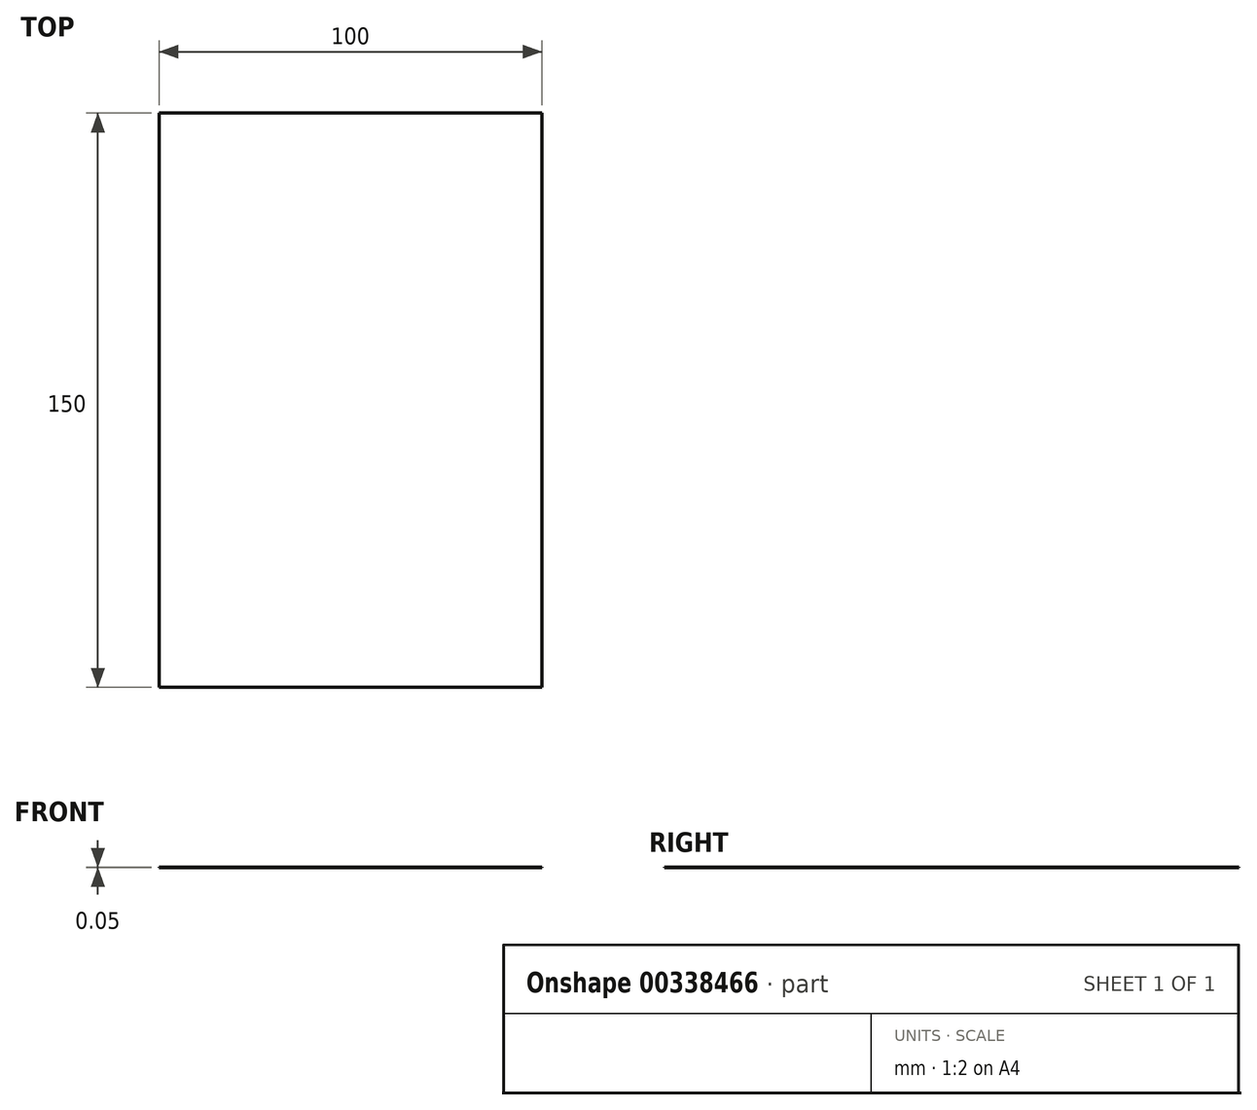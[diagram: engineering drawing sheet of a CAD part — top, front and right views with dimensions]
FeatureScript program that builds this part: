
annotation { "Feature Type Name" : "Feature", "Feature Type Description" : "" }
export const myFeature = defineFeature(function(context is Context, id is Id, definition is map)
    precondition{}
    {
        {
            var Q0;
            Q0=qCreatedBy(makeId("Top.planeOp"),FACE);
            var sketch = newSketch(context, id + "F0", { "sketchPlane" : qUnion([Q0])});
            skLineSegment(sketch, "E0.bottom", {"start": v(50, -75) * mm, "end": v(-50, -75) * mm});
            skLineSegment(sketch, "E0.top", {"start": v(50, 75) * mm, "end": v(-50, 75) * mm});
            skLineSegment(sketch, "E0.left", {"start": v(50, -75) * mm, "end": v(50, 75) * mm});
            skLineSegment(sketch, "E0.right", {"start": v(-50, -75) * mm, "end": v(-50, 75) * mm});
            skPoint(sketch, "E0.middle", {"position": v(0, 0) * mm});
            skSolve(sketch);
        }
        {
            var Q0;
            Q0 = qSketchRegion(id + "F0", true);
            extrude(context, id + "F1", {"entities" : qUnion([Q0]), "depth" : 0.05 * mm});
        }
    });
